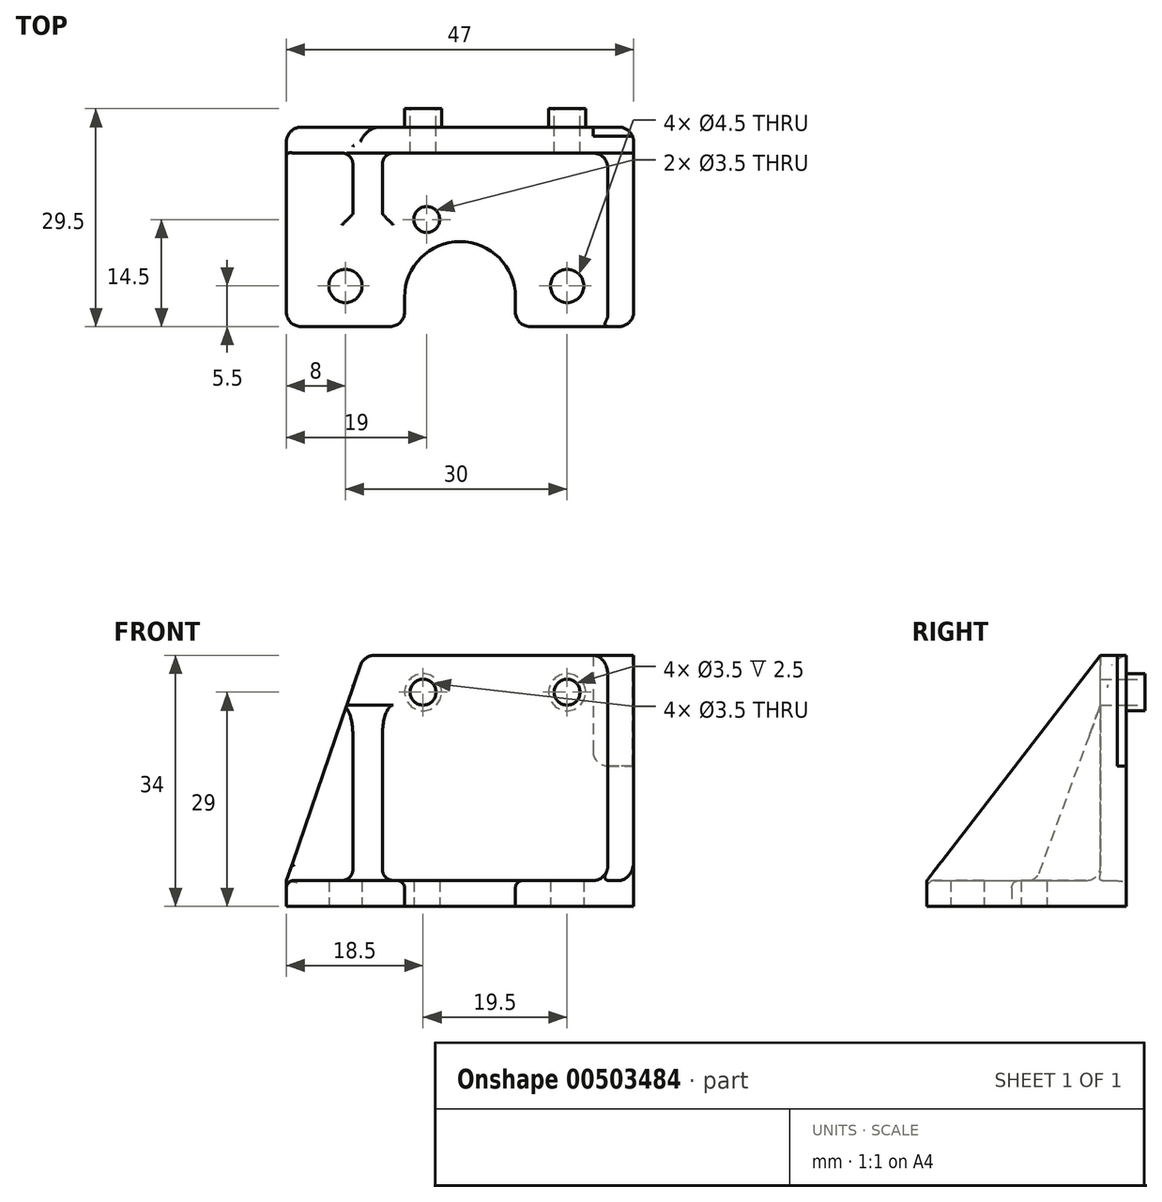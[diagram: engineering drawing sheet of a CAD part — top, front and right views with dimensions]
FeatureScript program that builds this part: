
annotation { "Feature Type Name" : "Feature", "Feature Type Description" : "" }
export const myFeature = defineFeature(function(context is Context, id is Id, definition is map)
    precondition{}
    {
        {
            var Q0;
            Q0=qCreatedBy(makeId("Top.planeOp"),FACE);
            var sketch = newSketch(context, id + "F0", { "sketchPlane" : qUnion([Q0])});
            skLineSegment(sketch, "E0.bottom", {"start": v(23.5, -13.5) * mm, "end": v(7.5, -13.5) * mm});
            skLineSegment(sketch, "E0.top", {"start": v(23.5, 13.5) * mm, "end": v(-23.5, 13.5) * mm});
            skLineSegment(sketch, "E0.left", {"start": v(23.5, -13.5) * mm, "end": v(23.5, 13.5) * mm});
            skLineSegment(sketch, "E0.right", {"start": v(-23.5, -13.5) * mm, "end": v(-23.5, 13.5) * mm});
            skPoint(sketch, "E0.middle", {"position": v(0, 0) * mm});
            skArc(sketch, "E1", {"start": v(7.5, -9.5) * mm, "mid": v(0, -2) * mm, "end": v(-7.5, -9.5) * mm});
            skLineSegment(sketch, "E2", {"start": v(-7.5, -13.5) * mm, "end": v(-7.5, -9.5) * mm});
            skLineSegment(sketch, "E3", {"start": v(7.5, -13.5) * mm, "end": v(7.5, -9.5) * mm});
            skLineSegment(sketch, "E4.trimOffspring", {"start": v(-7.5, -13.5) * mm, "end": v(-23.5, -13.5) * mm});
            skPoint(sketch, "E5.orphan", {"position": v(0, -13.5) * mm});
            skLineSegment(sketch, "E6", {"start": v(-23.5, -13.5) * mm, "end": v(-23.5, -8) * mm});
            skLineSegment(sketch, "E7", {"start": v(-23.5, -13.5) * mm, "end": v(-23.5, 0) * mm});
            skLineSegment(sketch, "E8", {"start": v(-23.5, -8) * mm, "end": v(-23.5, 1) * mm});
            skLineSegment(sketch, "E9", {"start": v(-23.5, 1) * mm, "end": v(25.69, 1) * mm, "construction": true});
            skLineSegment(sketch, "E10", {"start": v(-23.5, 1) * mm, "end": v(-4.5, 1) * mm});
            skCircle(sketch, "E11", {"center": v(-4.5, 1) * mm, "radius": 1.75 * mm});
            skLineSegment(sketch, "E12", {"start": v(-23.5, -8) * mm, "end": v(-15.5, -8) * mm, "construction": true});
            skCircle(sketch, "E13", {"center": v(-15.5, -8) * mm, "radius": 1.75 * mm});
            skLineSegment(sketch, "E14", {"start": v(-15.5, -8) * mm, "end": v(14.5, -8) * mm, "construction": true});
            skCircle(sketch, "E15", {"center": v(14.5, -8) * mm, "radius": 1.75 * mm});
            skSolve(sketch);
        }
        {
            var Q0;
            Q0 = qSketchRegion(id + "F0", true);
            extrude(context, id + "F1", {"entities" : qUnion([Q0]), "depth" : 3.5 * mm, "offsetDistance" : 25 * mm});
        }
        {
            var Q0;
            Q0=qCreatedBy(makeId("Front.planeOp"),FACE);
            var sketch = newSketch(context, id + "F2", { "sketchPlane" : qUnion([Q0])});
            skLineSegment(sketch, "E16", {"start": v(0, 0) * mm, "end": v(23.5, 0) * mm});
            skLineSegment(sketch, "E17", {"start": v(23.5, 0) * mm, "end": v(23.5, 34) * mm});
            skLineSegment(sketch, "E18", {"start": v(23.5, 34) * mm, "end": v(-13, 34) * mm});
            skLineSegment(sketch, "E19", {"start": v(0, 0) * mm, "end": v(-23.5, 0) * mm});
            skLineSegment(sketch, "E20", {"start": v(-23.5, 0) * mm, "end": v(-23.5, 3.5) * mm});
            skLineSegment(sketch, "E21", {"start": v(-23.5, 3.5) * mm, "end": v(-13, 34) * mm});
            skLineSegment(sketch, "E22", {"start": v(23.5, 34) * mm, "end": v(23.5, 29) * mm});
            skLineSegment(sketch, "E23", {"start": v(23.5, 29) * mm, "end": v(14.5, 29) * mm, "construction": true});
            skLineSegment(sketch, "E24", {"start": v(14.5, 29) * mm, "end": v(-5, 29) * mm, "construction": true});
            skCircle(sketch, "E25", {"center": v(-5, 29) * mm, "radius": 1.75 * mm});
            skCircle(sketch, "E26", {"center": v(14.5, 29) * mm, "radius": 1.75 * mm});
            skSolve(sketch);
        }
        {
            var Q0;
            Q0 = qSketchRegion(id + "F2", true);
            extrude(context, id + "F3", {"entities" : qUnion([Q0]), "endBound" : BoundingType.SYMMETRIC, "depth" : 3.5 * mm, "offsetDistance" : 25 * mm});
        }
        {
            var Q0;
            Q0=makeQuery(id+"F3.opExtrude","SWEPT_BODY",BODY,{"disambiguationData":[OSD([sQuery(id+"F2.wireOp",EDGE,"E16"),sQuery(id+"F2.wireOp",EDGE,"E17"),sQuery(id+"F2.wireOp",EDGE,"E18"),sQuery(id+"F2.wireOp",EDGE,"E19"),sQuery(id+"F2.wireOp",EDGE,"E20"),sQuery(id+"F2.wireOp",EDGE,"E21"),sQuery(id+"F2.wireOp",EDGE,"E22"),sQuery(id+"F2.wireOp",EDGE,"E25"),sQuery(id+"F2.wireOp",EDGE,"E26")])]});
            transform(context, id + "F4", {"entities" : qUnion([Q0]), "transformType" : TransformType.TRANSLATION_3D, "dx" : 0 * mm, "dy" : 11.75 * mm, "dz" : 0 * mm, "makeCopy" : false});
        }
        {
            var Q0;
            Q0=qCreatedBy(makeId("Right.planeOp"),FACE);
            var sketch = newSketch(context, id + "F5", { "sketchPlane" : qUnion([Q0])});
            skLineSegment(sketch, "E27", {"start": v(0, 0) * mm, "end": v(-13.5, 0) * mm});
            skLineSegment(sketch, "E28", {"start": v(-13.5, 0) * mm, "end": v(-13.5, 3.5) * mm});
            skLineSegment(sketch, "E29", {"start": v(0, 0) * mm, "end": v(13.5, 0) * mm});
            skLineSegment(sketch, "E30", {"start": v(13.5, 0) * mm, "end": v(13.5, 34) * mm});
            skLineSegment(sketch, "E31", {"start": v(13.5, 34) * mm, "end": v(10, 34) * mm});
            skLineSegment(sketch, "E32", {"start": v(10, 34) * mm, "end": v(-13.5, 3.5) * mm});
            skSolve(sketch);
        }
        {
            var Q0;
            Q0 = qSketchRegion(id + "F5", true);
            extrude(context, id + "F6", {"entities" : qUnion([Q0]), "endBound" : BoundingType.SYMMETRIC, "depth" : 3.5 * mm, "offsetDistance" : 25 * mm});
        }
        {
            var Q0;
            Q0=makeQuery(id+"F6.opExtrude","SWEPT_BODY",BODY,{"disambiguationData":[OSD([sQuery(id+"F5.wireOp",EDGE,"E27"),sQuery(id+"F5.wireOp",EDGE,"E28"),sQuery(id+"F5.wireOp",EDGE,"E29"),sQuery(id+"F5.wireOp",EDGE,"E30"),sQuery(id+"F5.wireOp",EDGE,"E31"),sQuery(id+"F5.wireOp",EDGE,"E32")])]});
            transform(context, id + "F7", {"entities" : qUnion([Q0]), "transformType" : TransformType.TRANSLATION_3D, "dx" : 21.75 * mm, "dy" : 0 * mm, "dz" : 0 * mm, "makeCopy" : false});
        }
        {
            var Q0;
            Q0=makeQuery(id+"F3.opExtrude","SWEPT_BODY",BODY,{"disambiguationData":[OSD([sQuery(id+"F2.wireOp",EDGE,"E16"),sQuery(id+"F2.wireOp",EDGE,"E17"),sQuery(id+"F2.wireOp",EDGE,"E18"),sQuery(id+"F2.wireOp",EDGE,"E19"),sQuery(id+"F2.wireOp",EDGE,"E20"),sQuery(id+"F2.wireOp",EDGE,"E21"),sQuery(id+"F2.wireOp",EDGE,"E22"),sQuery(id+"F2.wireOp",EDGE,"E25"),sQuery(id+"F2.wireOp",EDGE,"E26")])]});
            var Q1;
            Q1=makeQuery(id+"F1.opExtrude","SWEPT_BODY",BODY,{"disambiguationData":[OSD([sQuery(id+"F0.wireOp",EDGE,"E0.bottom"),sQuery(id+"F0.wireOp",EDGE,"E0.top"),sQuery(id+"F0.wireOp",EDGE,"E0.left"),sQuery(id+"F0.wireOp",EDGE,"E0.right"),sQuery(id+"F0.wireOp",EDGE,"E1"),sQuery(id+"F0.wireOp",EDGE,"E2"),sQuery(id+"F0.wireOp",EDGE,"E3"),sQuery(id+"F0.wireOp",EDGE,"E4.trimOffspring"),sQuery(id+"F0.wireOp",EDGE,"E7"),sQuery(id+"F0.wireOp",EDGE,"E8"),sQuery(id+"F0.wireOp",EDGE,"E11"),sQuery(id+"F0.wireOp",EDGE,"E13"),sQuery(id+"F0.wireOp",EDGE,"E15")])]});
            var Q2;
            Q2=makeQuery(id+"F6.opExtrude","SWEPT_BODY",BODY,{"disambiguationData":[OSD([sQuery(id+"F5.wireOp",EDGE,"E27"),sQuery(id+"F5.wireOp",EDGE,"E28"),sQuery(id+"F5.wireOp",EDGE,"E29"),sQuery(id+"F5.wireOp",EDGE,"E30"),sQuery(id+"F5.wireOp",EDGE,"E31"),sQuery(id+"F5.wireOp",EDGE,"E32")])]});
            booleanBodies(context, id + "F8", {"operationType" : BooleanOperationType.UNION, "tools" : qUnion([Q0, Q1, Q2])});
        }
        {
            var Q0;
            Q0=makeQuery(id+"F8.opBoolean","INTERSECT",EDGE,{"derivedFrom":[makeQuery(id+"F1.opExtrude","CAP_FACE",FACE,{"disambiguationData":[OSD([sQuery(id+"F0.wireOp",EDGE,"E0.bottom"),sQuery(id+"F0.wireOp",EDGE,"E0.top"),sQuery(id+"F0.wireOp",EDGE,"E0.left"),sQuery(id+"F0.wireOp",EDGE,"E0.right"),sQuery(id+"F0.wireOp",EDGE,"E1"),sQuery(id+"F0.wireOp",EDGE,"E2"),sQuery(id+"F0.wireOp",EDGE,"E3"),sQuery(id+"F0.wireOp",EDGE,"E4.trimOffspring"),sQuery(id+"F0.wireOp",EDGE,"E7"),sQuery(id+"F0.wireOp",EDGE,"E8"),sQuery(id+"F0.wireOp",EDGE,"E11"),sQuery(id+"F0.wireOp",EDGE,"E13"),sQuery(id+"F0.wireOp",EDGE,"E15")])],"isStart":false}),makeQuery(id+"F3.opExtrude","CAP_FACE",FACE,{"disambiguationData":[OSD([sQuery(id+"F2.wireOp",EDGE,"E16"),sQuery(id+"F2.wireOp",EDGE,"E17"),sQuery(id+"F2.wireOp",EDGE,"E18"),sQuery(id+"F2.wireOp",EDGE,"E19"),sQuery(id+"F2.wireOp",EDGE,"E20"),sQuery(id+"F2.wireOp",EDGE,"E21"),sQuery(id+"F2.wireOp",EDGE,"E22"),sQuery(id+"F2.wireOp",EDGE,"E25"),sQuery(id+"F2.wireOp",EDGE,"E26")])],"isStart":false})]});
            var Q1;
            Q1=makeQuery(id+"F8.opBoolean","INTERSECT",EDGE,{"derivedFrom":[makeQuery(id+"F1.opExtrude","CAP_FACE",FACE,{"disambiguationData":[OSD([sQuery(id+"F0.wireOp",EDGE,"E0.bottom"),sQuery(id+"F0.wireOp",EDGE,"E0.top"),sQuery(id+"F0.wireOp",EDGE,"E0.left"),sQuery(id+"F0.wireOp",EDGE,"E0.right"),sQuery(id+"F0.wireOp",EDGE,"E1"),sQuery(id+"F0.wireOp",EDGE,"E2"),sQuery(id+"F0.wireOp",EDGE,"E3"),sQuery(id+"F0.wireOp",EDGE,"E4.trimOffspring"),sQuery(id+"F0.wireOp",EDGE,"E7"),sQuery(id+"F0.wireOp",EDGE,"E8"),sQuery(id+"F0.wireOp",EDGE,"E11"),sQuery(id+"F0.wireOp",EDGE,"E13"),sQuery(id+"F0.wireOp",EDGE,"E15")])],"isStart":false}),makeQuery(id+"F6.opExtrude","CAP_FACE",FACE,{"disambiguationData":[OSD([sQuery(id+"F5.wireOp",EDGE,"E27"),sQuery(id+"F5.wireOp",EDGE,"E28"),sQuery(id+"F5.wireOp",EDGE,"E29"),sQuery(id+"F5.wireOp",EDGE,"E30"),sQuery(id+"F5.wireOp",EDGE,"E31"),sQuery(id+"F5.wireOp",EDGE,"E32")])],"isStart":true})]});
            var Q2;
            Q2=makeQuery(id+"F8.opBoolean","INTERSECT",EDGE,{"derivedFrom":[makeQuery(id+"F3.opExtrude","CAP_FACE",FACE,{"disambiguationData":[OSD([sQuery(id+"F2.wireOp",EDGE,"E16"),sQuery(id+"F2.wireOp",EDGE,"E17"),sQuery(id+"F2.wireOp",EDGE,"E18"),sQuery(id+"F2.wireOp",EDGE,"E19"),sQuery(id+"F2.wireOp",EDGE,"E20"),sQuery(id+"F2.wireOp",EDGE,"E21"),sQuery(id+"F2.wireOp",EDGE,"E22"),sQuery(id+"F2.wireOp",EDGE,"E25"),sQuery(id+"F2.wireOp",EDGE,"E26")])],"isStart":false}),makeQuery(id+"F6.opExtrude","CAP_FACE",FACE,{"disambiguationData":[OSD([sQuery(id+"F5.wireOp",EDGE,"E27"),sQuery(id+"F5.wireOp",EDGE,"E28"),sQuery(id+"F5.wireOp",EDGE,"E29"),sQuery(id+"F5.wireOp",EDGE,"E30"),sQuery(id+"F5.wireOp",EDGE,"E31"),sQuery(id+"F5.wireOp",EDGE,"E32")])],"isStart":true})]});
            fillet(context, id + "F9", {"entities" : qUnion([Q0, Q1, Q2]), "radius" : 2 * mm, "tangentPropagation" : true, "allowEdgeOverflow" : false});
        }
        {
            var Q0;
            Q0=qCreatedBy(makeId("Top.planeOp"),FACE);
            var sketch = newSketch(context, id + "F10", { "sketchPlane" : qUnion([Q0])});
            skLineSegment(sketch, "E33", {"start": v(0, 0) * mm, "end": v(0, 13.5) * mm, "construction": true});
            skLineSegment(sketch, "E34", {"start": v(0, 13.5) * mm, "end": v(18, 13.5) * mm, "construction": true});
            skLineSegment(sketch, "E35", {"start": v(18, 13.5) * mm, "end": v(18, 12.3) * mm});
            skLineSegment(sketch, "E36", {"start": v(18, 12.3) * mm, "end": v(24, 12.3) * mm});
            skLineSegment(sketch, "E37", {"start": v(24, 12.3) * mm, "end": v(24, 13.5) * mm});
            skLineSegment(sketch, "E38", {"start": v(24, 13.5) * mm, "end": v(18, 13.5) * mm});
            skSolve(sketch);
        }
        {
            var Q0;
            Q0 = qSketchRegion(id + "F10", true);
            extrude(context, id + "F11", {"entities" : qUnion([Q0]), "depth" : 15 * mm, "offsetDistance" : 25 * mm});
        }
        {
            var Q0;
            Q0=makeQuery(id+"F11.opExtrude","SWEPT_BODY",BODY,{"disambiguationData":[OSD([sQuery(id+"F10.wireOp",EDGE,"E35"),sQuery(id+"F10.wireOp",EDGE,"E36"),sQuery(id+"F10.wireOp",EDGE,"E37"),sQuery(id+"F10.wireOp",EDGE,"E38")])]});
            transform(context, id + "F12", {"entities" : qUnion([Q0]), "transformType" : TransformType.TRANSLATION_3D, "dx" : 0 * mm, "dy" : 0 * mm, "dz" : 19 * mm, "makeCopy" : false});
        }
        {
            var Q0;
            Q0=makeQuery(id+"F11.opExtrude","SWEPT_BODY",BODY,{"disambiguationData":[OSD([sQuery(id+"F10.wireOp",EDGE,"E35"),sQuery(id+"F10.wireOp",EDGE,"E36"),sQuery(id+"F10.wireOp",EDGE,"E37"),sQuery(id+"F10.wireOp",EDGE,"E38")])]});
            var Q1;
            Q1=makeQuery(id+"F3.opExtrude","SWEPT_BODY",BODY,{"disambiguationData":[OSD([sQuery(id+"F2.wireOp",EDGE,"E16"),sQuery(id+"F2.wireOp",EDGE,"E17"),sQuery(id+"F2.wireOp",EDGE,"E18"),sQuery(id+"F2.wireOp",EDGE,"E19"),sQuery(id+"F2.wireOp",EDGE,"E20"),sQuery(id+"F2.wireOp",EDGE,"E21"),sQuery(id+"F2.wireOp",EDGE,"E22"),sQuery(id+"F2.wireOp",EDGE,"E25"),sQuery(id+"F2.wireOp",EDGE,"E26")])]});
            booleanBodies(context, id + "F13", {"operationType" : BooleanOperationType.SUBTRACTION, "tools" : qUnion([Q0]), "targets" : qUnion([Q1])});
        }
        {
            var Q0;
            Q0=makeQuery(id+"F13.opBoolean","COPY",EDGE,{"derivedFrom":makeQuery(id+"F11.opExtrude","CAP_EDGE",EDGE,{"disambiguationData":[OSD([sQuery(id+"F10.wireOp",EDGE,"E35")])],"isStart":true})});
            var Q1;
            Q1=makeQuery(id+"F3.opExtrude","SWEPT_EDGE",EDGE,{"disambiguationData":[OSD([sQuery(id+"F2.wireOp",EDGE,"E18"),sQuery(id+"F2.wireOp",EDGE,"E21")])]});
            var Q2;
            Q2=makeQuery(id+"F1.opExtrude","SWEPT_EDGE",EDGE,{"disambiguationData":[OSD([sQuery(id+"F0.wireOp",EDGE,"E4.trimOffspring"),sQuery(id+"F0.wireOp",EDGE,"E7")])]});
            var Q3;
            Q3=makeQuery(id+"F1.opExtrude","SWEPT_EDGE",EDGE,{"disambiguationData":[OSD([sQuery(id+"F0.wireOp",EDGE,"E0.bottom"),sQuery(id+"F0.wireOp",EDGE,"E0.left")])]});
            var Q4;
            Q4=makeQuery(id+"F3.opExtrude","CAP_EDGE",EDGE,{"disambiguationData":[OSD([sQuery(id+"F2.wireOp",EDGE,"E17"),sQuery(id+"F2.wireOp",EDGE,"E22")])],"isStart":true});
            var Q5;
            Q5=makeQuery(id+"F3.opExtrude","CAP_EDGE",EDGE,{"disambiguationData":[OSD([sQuery(id+"F2.wireOp",EDGE,"E20")])],"isStart":true});
            var Q6;
            Q6=makeQuery(id+"F3.opExtrude","CAP_EDGE",EDGE,{"disambiguationData":[OSD([sQuery(id+"F2.wireOp",EDGE,"E21")])],"isStart":true});
            var Q7;
            Q7=makeQuery(id+"F1.opExtrude","SWEPT_EDGE",EDGE,{"disambiguationData":[OSD([sQuery(id+"F0.wireOp",EDGE,"E2"),sQuery(id+"F0.wireOp",EDGE,"E4.trimOffspring")])]});
            var Q8;
            Q8=makeQuery(id+"F1.opExtrude","SWEPT_EDGE",EDGE,{"disambiguationData":[OSD([sQuery(id+"F0.wireOp",EDGE,"E0.bottom"),sQuery(id+"F0.wireOp",EDGE,"E3")])]});
            fillet(context, id + "F14", {"entities" : qUnion([Q0, Q1, Q2, Q3, Q4, Q5, Q6, Q7, Q8]), "radius" : 2 * mm, "tangentPropagation" : true, "allowEdgeOverflow" : false});
        }
        {
            var Q0;
            Q0=makeQuery(id+"F1.opExtrude","CAP_EDGE",EDGE,{"disambiguationData":[OSD([sQuery(id+"F0.wireOp",EDGE,"E0.right"),sQuery(id+"F0.wireOp",EDGE,"E7"),sQuery(id+"F0.wireOp",EDGE,"E8")])],"isStart":false});
            var Q1;
            Q1=makeQuery(id+"F8.opBoolean","SPLIT",EDGE,{"derivedFrom":makeQuery(id+"F1.opExtrude","CAP_EDGE",EDGE,{"disambiguationData":[OSD([sQuery(id+"F0.wireOp",EDGE,"E0.bottom")])],"isStart":false})});
            var Q2;
            Q2=makeQuery(id+"F1.opExtrude","CAP_EDGE",EDGE,{"disambiguationData":[OSD([sQuery(id+"F0.wireOp",EDGE,"E1")])],"isStart":false});
            fillet(context, id + "F15", {"entities" : qUnion([Q0, Q1, Q2]), "radius" : 1 * mm, "tangentPropagation" : true, "allowEdgeOverflow" : false});
        }
        {
            var Q0;
            Q0=qCreatedBy(makeId("Right.planeOp"),FACE);
            var sketch = newSketch(context, id + "F16", { "sketchPlane" : qUnion([Q0])});
            skLineSegment(sketch, "E39", {"start": v(0, 0) * mm, "end": v(11, 0) * mm});
            skLineSegment(sketch, "E40", {"start": v(11, 0) * mm, "end": v(11, 30) * mm});
            skLineSegment(sketch, "E41", {"start": v(11, 30) * mm, "end": v(0, 0) * mm});
            skSolve(sketch);
        }
        {
            var Q0;
            Q0 = qSketchRegion(id + "F16", true);
            extrude(context, id + "F17", {"entities" : qUnion([Q0]), "depth" : 4 * mm, "offsetDistance" : 25 * mm});
        }
        {
            var Q0;
            Q0=makeQuery(id+"F17.opExtrude","SWEPT_BODY",BODY,{"disambiguationData":[OSD([sQuery(id+"F16.wireOp",EDGE,"E39"),sQuery(id+"F16.wireOp",EDGE,"E40"),sQuery(id+"F16.wireOp",EDGE,"E41")])]});
            transform(context, id + "F18", {"entities" : qUnion([Q0]), "transformType" : TransformType.TRANSLATION_3D, "dx" : -14.5 * mm, "dy" : 0 * mm, "dz" : 0 * mm, "makeCopy" : false});
        }
        {
            var Q0;
            Q0=makeQuery(id+"F17.opExtrude","SWEPT_BODY",BODY,{"disambiguationData":[OSD([sQuery(id+"F16.wireOp",EDGE,"E39"),sQuery(id+"F16.wireOp",EDGE,"E40"),sQuery(id+"F16.wireOp",EDGE,"E41")])]});
            var Q1;
            Q1=makeQuery(id+"F3.opExtrude","SWEPT_BODY",BODY,{"disambiguationData":[OSD([sQuery(id+"F2.wireOp",EDGE,"E16"),sQuery(id+"F2.wireOp",EDGE,"E17"),sQuery(id+"F2.wireOp",EDGE,"E18"),sQuery(id+"F2.wireOp",EDGE,"E19"),sQuery(id+"F2.wireOp",EDGE,"E20"),sQuery(id+"F2.wireOp",EDGE,"E21"),sQuery(id+"F2.wireOp",EDGE,"E22"),sQuery(id+"F2.wireOp",EDGE,"E25"),sQuery(id+"F2.wireOp",EDGE,"E26")])]});
            booleanBodies(context, id + "F19", {"operationType" : BooleanOperationType.UNION, "tools" : qUnion([Q0, Q1])});
        }
        {
            var Q0;
            Q0=makeQuery(id+"F19.opBoolean","INTERSECT",EDGE,{"derivedFrom":[makeQuery(id+"F3.opExtrude","CAP_FACE",FACE,{"disambiguationData":[OSD([sQuery(id+"F2.wireOp",EDGE,"E16"),sQuery(id+"F2.wireOp",EDGE,"E17"),sQuery(id+"F2.wireOp",EDGE,"E18"),sQuery(id+"F2.wireOp",EDGE,"E19"),sQuery(id+"F2.wireOp",EDGE,"E20"),sQuery(id+"F2.wireOp",EDGE,"E21"),sQuery(id+"F2.wireOp",EDGE,"E22"),sQuery(id+"F2.wireOp",EDGE,"E25"),sQuery(id+"F2.wireOp",EDGE,"E26")])],"isStart":false}),makeQuery(id+"F17.opExtrude","CAP_FACE",FACE,{"disambiguationData":[OSD([sQuery(id+"F16.wireOp",EDGE,"E39"),sQuery(id+"F16.wireOp",EDGE,"E40"),sQuery(id+"F16.wireOp",EDGE,"E41")])],"isStart":true})]});
            var Q1;
            Q1=makeQuery(id+"F19.opBoolean","INTERSECT",EDGE,{"derivedFrom":[makeQuery(id+"F3.opExtrude","CAP_FACE",FACE,{"disambiguationData":[OSD([sQuery(id+"F2.wireOp",EDGE,"E16"),sQuery(id+"F2.wireOp",EDGE,"E17"),sQuery(id+"F2.wireOp",EDGE,"E18"),sQuery(id+"F2.wireOp",EDGE,"E19"),sQuery(id+"F2.wireOp",EDGE,"E20"),sQuery(id+"F2.wireOp",EDGE,"E21"),sQuery(id+"F2.wireOp",EDGE,"E22"),sQuery(id+"F2.wireOp",EDGE,"E25"),sQuery(id+"F2.wireOp",EDGE,"E26")])],"isStart":false}),makeQuery(id+"F17.opExtrude","CAP_FACE",FACE,{"disambiguationData":[OSD([sQuery(id+"F16.wireOp",EDGE,"E39"),sQuery(id+"F16.wireOp",EDGE,"E40"),sQuery(id+"F16.wireOp",EDGE,"E41")])],"isStart":false})]});
            var Q2;
            Q2=makeQuery(id+"F19.opBoolean","INTERSECT",EDGE,{"derivedFrom":[makeQuery(id+"F1.opExtrude","CAP_FACE",FACE,{"disambiguationData":[OSD([sQuery(id+"F0.wireOp",EDGE,"E0.bottom"),sQuery(id+"F0.wireOp",EDGE,"E0.top"),sQuery(id+"F0.wireOp",EDGE,"E0.left"),sQuery(id+"F0.wireOp",EDGE,"E0.right"),sQuery(id+"F0.wireOp",EDGE,"E1"),sQuery(id+"F0.wireOp",EDGE,"E2"),sQuery(id+"F0.wireOp",EDGE,"E3"),sQuery(id+"F0.wireOp",EDGE,"E4.trimOffspring"),sQuery(id+"F0.wireOp",EDGE,"E7"),sQuery(id+"F0.wireOp",EDGE,"E8"),sQuery(id+"F0.wireOp",EDGE,"E11"),sQuery(id+"F0.wireOp",EDGE,"E13"),sQuery(id+"F0.wireOp",EDGE,"E15")])],"isStart":false}),makeQuery(id+"F17.opExtrude","SWEPT_FACE",FACE,{"disambiguationData":[OSD([sQuery(id+"F16.wireOp",EDGE,"E41")])]})]});
            fillet(context, id + "F20", {"entities" : qUnion([Q0, Q1, Q2]), "radius" : 1.5 * mm, "tangentPropagation" : true, "allowEdgeOverflow" : false});
        }
        {
            var Q0;
            Q0=qCreatedBy(makeId("Front.planeOp"),FACE);
            var sketch = newSketch(context, id + "F21", { "sketchPlane" : qUnion([Q0])});
            skLineSegment(sketch, "E42", {"start": v(0, 0) * mm, "end": v(0, 29) * mm});
            skLineSegment(sketch, "E43", {"start": v(0, 29) * mm, "end": v(-5, 29) * mm});
            skLineSegment(sketch, "E44", {"start": v(0, 29) * mm, "end": v(14.5, 29) * mm});
            skCircle(sketch, "E45", {"center": v(-5, 29) * mm, "radius": 1.75 * mm});
            skCircle(sketch, "E46", {"center": v(14.5, 29) * mm, "radius": 1.75 * mm});
            skCircle(sketch, "E47", {"center": v(-5, 29) * mm, "radius": 2.5 * mm});
            skCircle(sketch, "E48", {"center": v(14.5, 29) * mm, "radius": 2.5 * mm});
            skSolve(sketch);
        }
        {
            var Q0;
            Q0 = qSketchRegion(id + "F21", true);
            extrude(context, id + "F22", {"entities" : qUnion([Q0]), "depth" : 2.5 * mm, "offsetDistance" : 25 * mm});
        }
        {
            var Q0;
            Q0=makeQuery(id+"F22.opExtrude","SWEPT_BODY",BODY,{"disambiguationData":[OSD([sQuery(id+"F21.wireOp",EDGE,"E46"),sQuery(id+"F21.wireOp",EDGE,"E48")])]});
            var Q1;
            Q1=makeQuery(id+"F22.opExtrude","SWEPT_BODY",BODY,{"disambiguationData":[OSD([sQuery(id+"F21.wireOp",EDGE,"E45"),sQuery(id+"F21.wireOp",EDGE,"E47")])]});
            transform(context, id + "F23", {"entities" : qUnion([Q0, Q1]), "transformType" : TransformType.TRANSLATION_3D, "dx" : 0 * mm, "dy" : 16 * mm, "dz" : 0 * mm, "makeCopy" : false});
        }
        {
            var Q0;
            Q0=qCreatedBy(makeId("Top.planeOp"),FACE);
            var sketch = newSketch(context, id + "F24", { "sketchPlane" : qUnion([Q0])});
            skLineSegment(sketch, "E49", {"start": v(0, 0) * mm, "end": v(0, -8) * mm});
            skLineSegment(sketch, "E50", {"start": v(0, -8) * mm, "end": v(-15.5, -8) * mm});
            skLineSegment(sketch, "E51", {"start": v(0, -8) * mm, "end": v(14.5, -8) * mm});
            skCircle(sketch, "E52", {"center": v(-15.5, -8) * mm, "radius": 2.25 * mm});
            skCircle(sketch, "E53", {"center": v(14.5, -8) * mm, "radius": 2.25 * mm});
            skSolve(sketch);
        }
        {
            var Q0;
            Q0 = qSketchRegion(id + "F24", true);
            extrude(context, id + "F25", {"entities" : qUnion([Q0]), "depth" : 25 * mm, "offsetDistance" : 25 * mm});
        }
        {
            var Q0;
            Q0=makeQuery(id+"F25.opExtrude","SWEPT_BODY",BODY,{"disambiguationData":[OSD([sQuery(id+"F24.wireOp",EDGE,"E52")])]});
            var Q1;
            Q1=makeQuery(id+"F25.opExtrude","SWEPT_BODY",BODY,{"disambiguationData":[OSD([sQuery(id+"F24.wireOp",EDGE,"E53")])]});
            var Q2;
            Q2=makeQuery(id+"F17.opExtrude","SWEPT_BODY",BODY,{"disambiguationData":[OSD([sQuery(id+"F16.wireOp",EDGE,"E39"),sQuery(id+"F16.wireOp",EDGE,"E40"),sQuery(id+"F16.wireOp",EDGE,"E41")])]});
            booleanBodies(context, id + "F26", {"operationType" : BooleanOperationType.SUBTRACTION, "tools" : qUnion([Q0, Q1]), "targets" : qUnion([Q2])});
        }
    });
